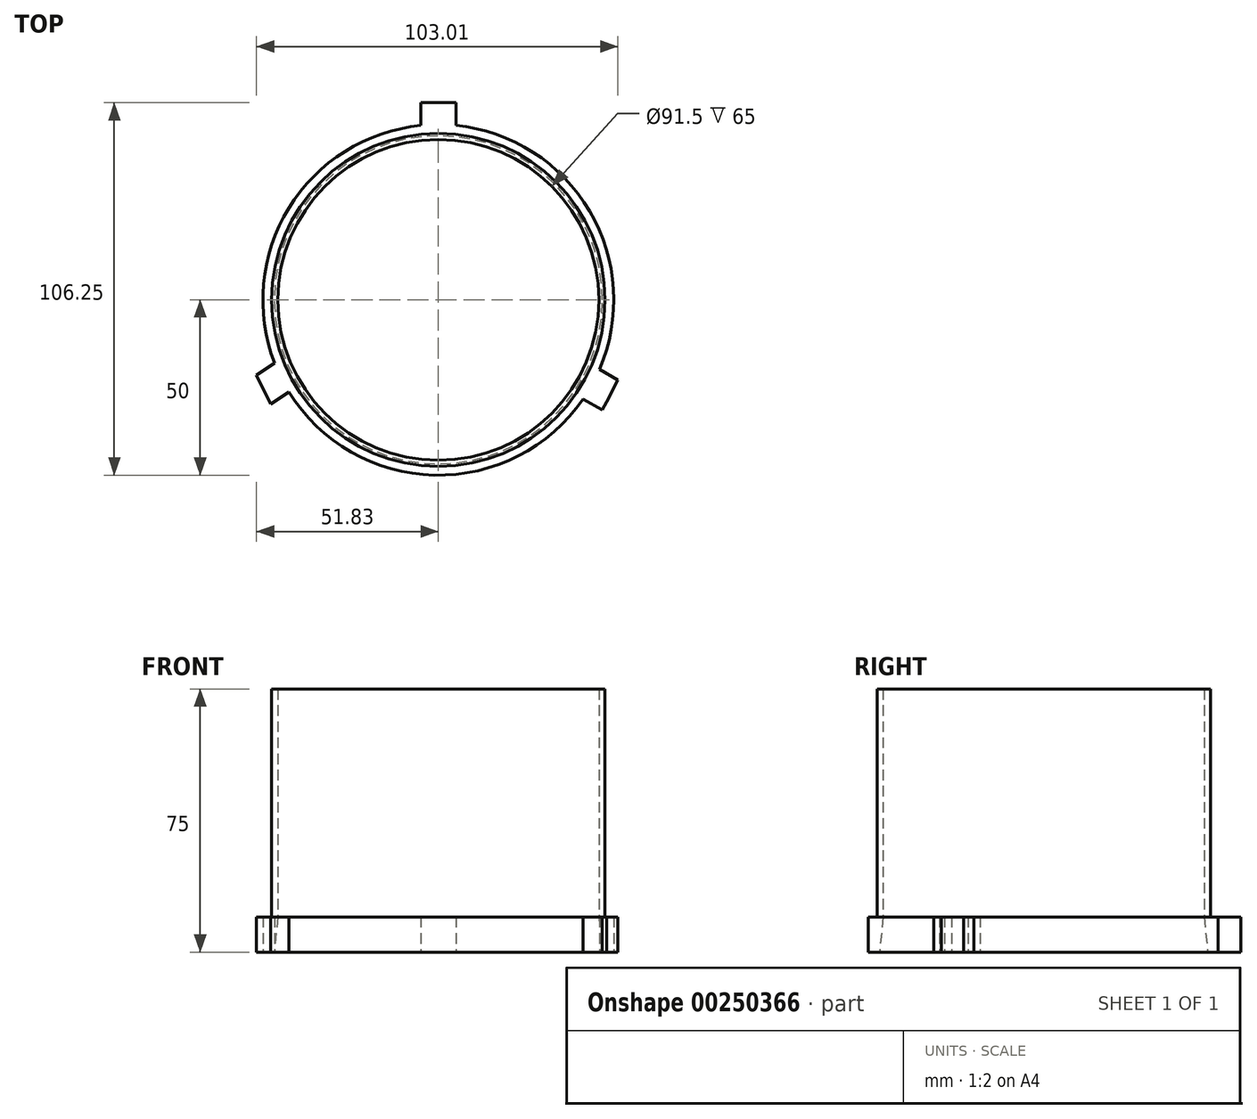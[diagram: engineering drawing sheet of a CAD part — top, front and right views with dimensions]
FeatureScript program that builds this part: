
annotation { "Feature Type Name" : "Feature", "Feature Type Description" : "" }
export const myFeature = defineFeature(function(context is Context, id is Id, definition is map)
    precondition{}
    {
        {
            var Q0;
            Q0=qCreatedBy(makeId("Top.planeOp"),FACE);
            var sketch = newSketch(context, id + "F0", { "sketchPlane" : qUnion([Q0])});
            skCircle(sketch, "E0", {"center": v(0, 0) * mm, "radius": 50 * mm});
            skCircle(sketch, "E1", {"center": v(0, 0) * mm, "radius": 45.75 * mm});
            skLineSegment(sketch, "E2.bottom", {"start": v(-5, 49.75) * mm, "end": v(5, 49.75) * mm});
            skLineSegment(sketch, "E2.top", {"start": v(-5, 56.25) * mm, "end": v(5, 56.25) * mm});
            skLineSegment(sketch, "E2.left", {"start": v(-5, 49.75) * mm, "end": v(-5, 56.25) * mm});
            skLineSegment(sketch, "E2.right", {"start": v(5, 49.75) * mm, "end": v(5, 56.25) * mm});
            skCircle(sketch, "E3", {"center": v(0, 0) * mm, "radius": 47.5 * mm});
            skLineSegment(sketch, "E4", {"start": v(51.18, -22.83) * mm, "end": v(47.9, -29.1) * mm});
            skLineSegment(sketch, "E5", {"start": v(51.18, -22.83) * mm, "end": v(45.89, -19.86) * mm});
            skLineSegment(sketch, "E6", {"start": v(42.53, -26.3) * mm, "end": v(45.89, -19.86) * mm});
            skLineSegment(sketch, "E7", {"start": v(-51.83, -21.5) * mm, "end": v(-46.63, -18.06) * mm});
            skLineSegment(sketch, "E8", {"start": v(-51.83, -21.5) * mm, "end": v(-47.74, -29.73) * mm});
            skLineSegment(sketch, "E9", {"start": v(-47.74, -29.73) * mm, "end": v(-42.53, -26.3) * mm});
            skLineSegment(sketch, "E10", {"start": v(-42.53, -26.3) * mm, "end": v(-46.63, -18.06) * mm});
            skLineSegment(sketch, "E11", {"start": v(47.9, -29.1) * mm, "end": v(46.67, -31.32) * mm});
            skLineSegment(sketch, "E12", {"start": v(46.67, -31.32) * mm, "end": v(41.24, -28.27) * mm});
            skLineSegment(sketch, "E13", {"start": v(41.24, -28.27) * mm, "end": v(42.53, -26.3) * mm});
            skSolve(sketch);
        }
        {
            var Q0;
            Q0 = qSketchRegion(id + "F0", true);
            extrude(context, id + "F1", {"entities" : qUnion([Q0]), "depth" : 10 * mm});
        }
        {
            var Q0;
            Q0=makeQuery(id+"F0.imprint","IMPRINT",FACE,{"disambiguationData":[TD([[makeQuery(id+"F0.imprint","IMPRINT",EDGE,{"derivedFrom":sQuery(id+"F0.wireOp",EDGE,"E1")}),-1.0]])]});
            extrude(context, id + "F2", {"entities" : qUnion([Q0]), "operationType" : NewBodyOperationType.ADD, "depth" : 75 * mm});
        }
        {
            var Q0;
            Q0=makeQuery(id+"F2.opExtrude","CAP_EDGE",EDGE,{"disambiguationData":[OSD([sQuery(id+"F0.wireOp",EDGE,"E1")])],"isStart":true});
            chamfer(context, id + "F3", {"entities" : qUnion([Q0]), "chamferType" : ChamferType.TWO_OFFSETS, "width1" : 1 * mm, "oppositeDirection" : false, "width2" : 10 * mm, "tangentPropagation" : true});
        }
    });
